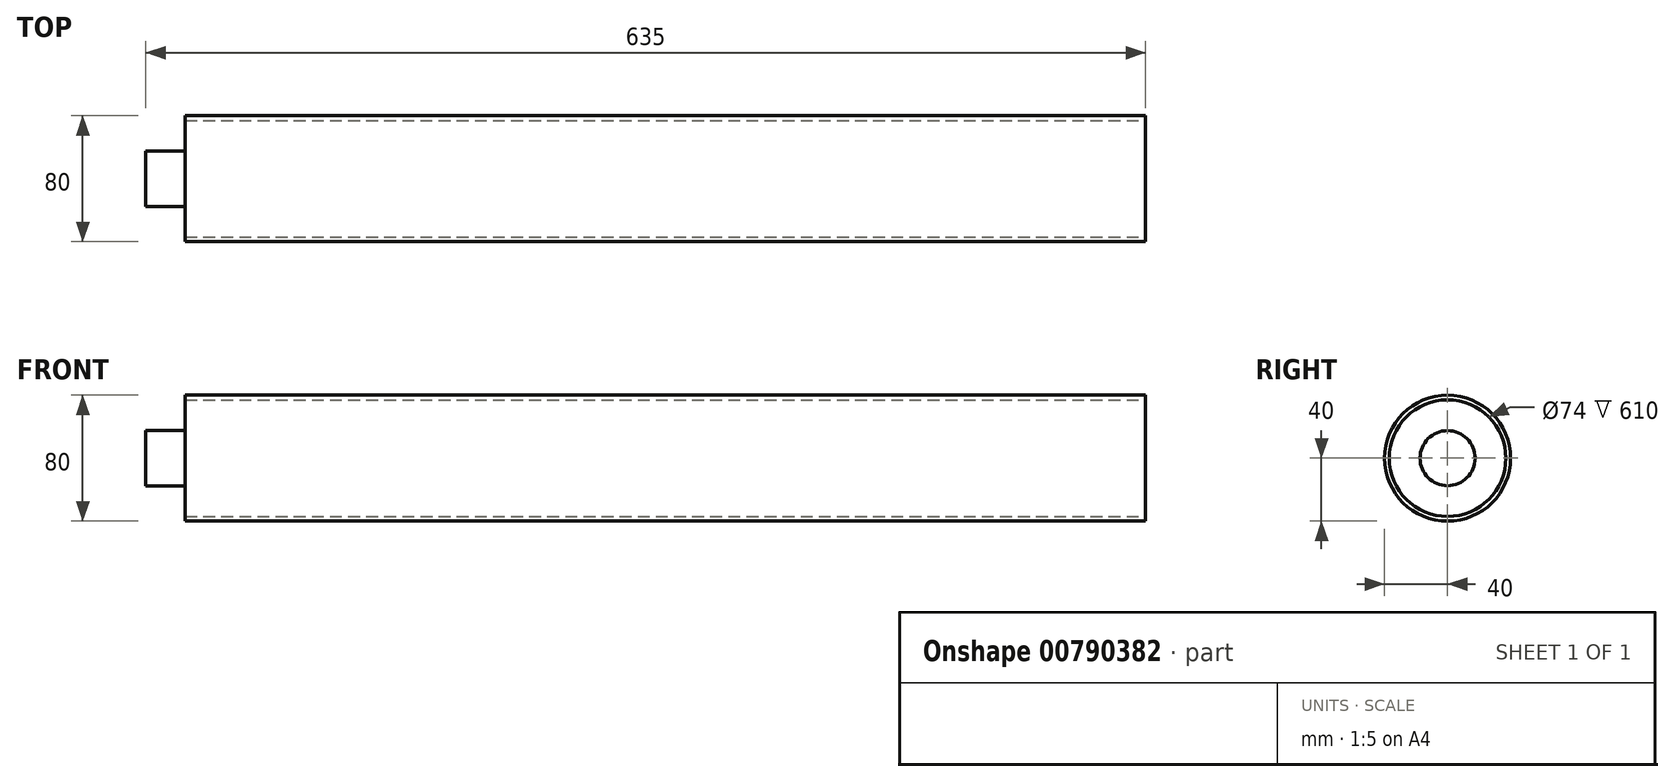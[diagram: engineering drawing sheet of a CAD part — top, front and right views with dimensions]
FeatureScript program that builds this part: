
annotation { "Feature Type Name" : "Feature", "Feature Type Description" : "" }
export const myFeature = defineFeature(function(context is Context, id is Id, definition is map)
    precondition{}
    {
        {
            var Q0;
            Q0=qCreatedBy(makeId("Top.planeOp"),FACE);
            var sketch = newSketch(context, id + "F0", { "sketchPlane" : qUnion([Q0])});
            skLineSegment(sketch, "E0.bottom", {"start": v(-305, 40) * mm, "end": v(305, 40) * mm});
            skLineSegment(sketch, "E0.top", {"start": v(-305, 37) * mm, "end": v(305, 37) * mm});
            skLineSegment(sketch, "E0.left", {"start": v(-305, 40) * mm, "end": v(-305, 37) * mm});
            skLineSegment(sketch, "E0.right", {"start": v(305, 40) * mm, "end": v(305, 37) * mm});
            skPoint(sketch, "E1", {"position": v(0, 40) * mm});
            skLineSegment(sketch, "E2", {"start": v(0, 0) * mm, "end": v(-92.87, 0) * mm, "construction": true});
            skLineSegment(sketch, "E3.bottom", {"start": v(-305, 37) * mm, "end": v(-275, 37) * mm});
            skLineSegment(sketch, "E3.top", {"start": v(-305, 0) * mm, "end": v(-275, 0) * mm});
            skLineSegment(sketch, "E3.left", {"start": v(-305, 37) * mm, "end": v(-305, 0) * mm});
            skLineSegment(sketch, "E3.right", {"start": v(-275, 37) * mm, "end": v(-275, 0) * mm});
            skSolve(sketch);
        }
        {
            var Q0;
            Q0=makeQuery(id+"F0.imprint","IMPRINT",FACE,{"disambiguationData":[TD([[makeQuery(id+"F0.imprint","IMPRINT",EDGE,{"derivedFrom":sQuery(id+"F0.wireOp",EDGE,"E0.bottom")}),-1.0]])]});
            var Q1;
            Q1=makeQuery(id+"F0.imprint","IMPRINT",FACE,{"disambiguationData":[TD([[makeQuery(id+"F0.imprint","IMPRINT",EDGE,{"derivedFrom":sQuery(id+"F0.wireOp",EDGE,"E3.bottom")}),-1.0]])]});
            var Q2;
            Q2=sQuery(id+"F0.wireOp",EDGE,"E2");
            revolve(context, id + "F1", {"surfaceOperationType" : NewSurfaceOperationType.NEW, "entities" : qUnion([Q0, Q1]), "axis" : qUnion([Q2]), "revolveType" : RevolveType.FULL});
        }
        {
            var Q0;
            Q0=makeQuery(id+"F1.opRevolve","SWEPT_FACE",FACE,{"disambiguationData":[OSD([sQuery(id+"F0.wireOp",EDGE,"E0.left"),sQuery(id+"F0.wireOp",EDGE,"E3.left")])]});
            var sketch = newSketch(context, id + "F2", { "sketchPlane" : qUnion([Q0])});
            skCircle(sketch, "E4", {"center": v(0, 0) * mm, "radius": 17.5 * mm});
            skSolve(sketch);
        }
        {
            var Q0;
            Q0=makeQuery(id+"F2.imprint","IMPRINT",FACE,{"disambiguationData":[TD([[makeQuery(id+"F2.imprint","IMPRINT",EDGE,{"derivedFrom":sQuery(id+"F2.wireOp",EDGE,"E4")}),1.0]])]});
            extrude(context, id + "F3", {"entities" : qUnion([Q0]), "operationType" : NewBodyOperationType.ADD, "depth" : 25 * mm, "offsetDistance" : 25 * mm});
        }
    });
